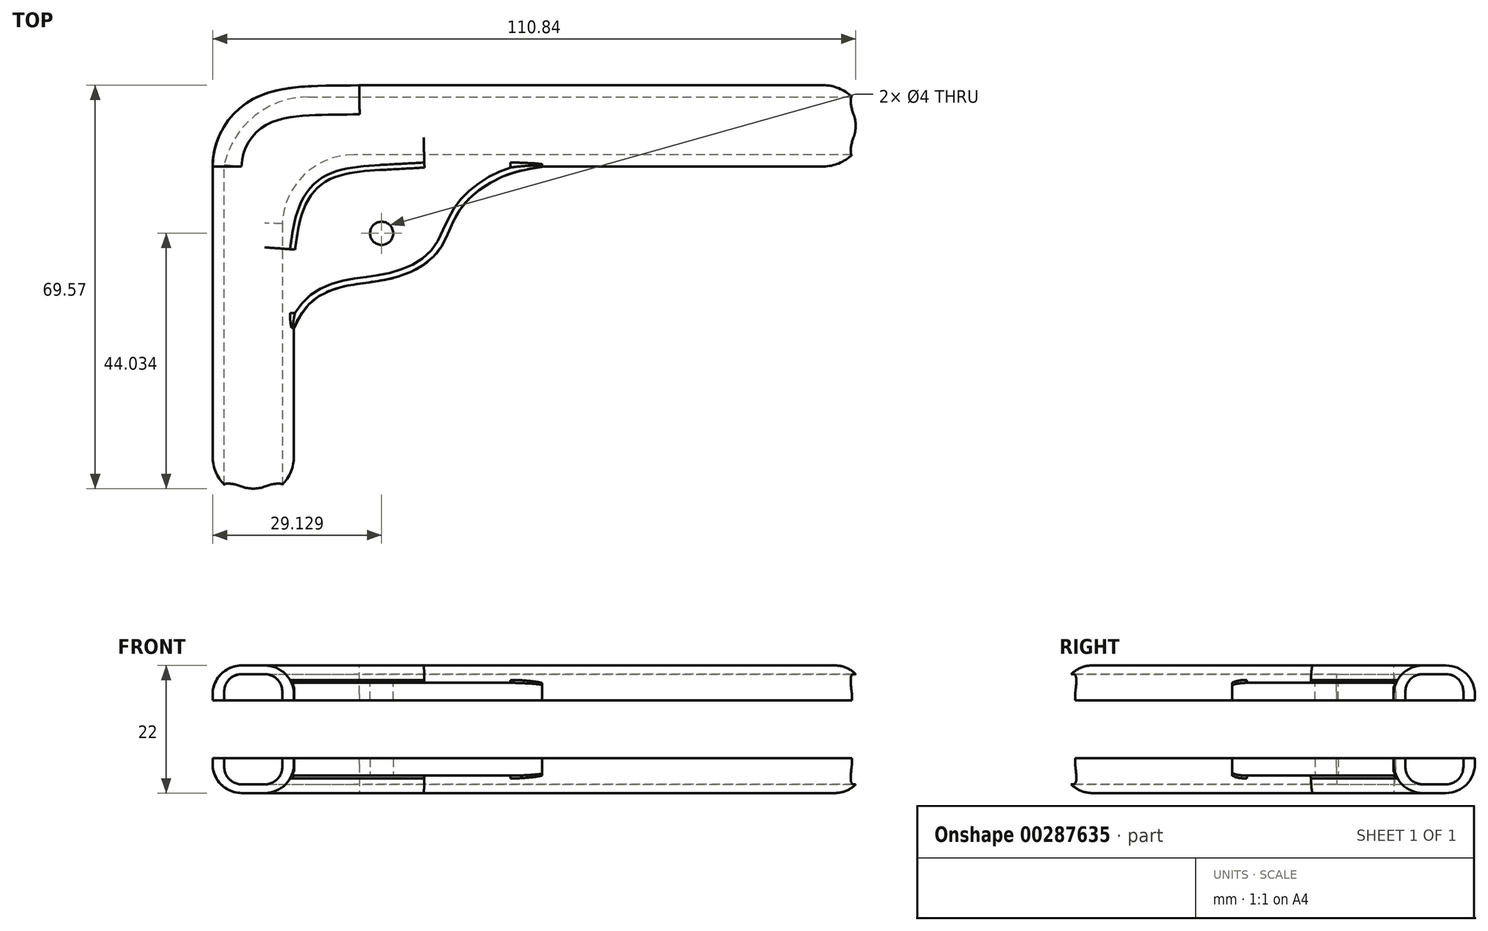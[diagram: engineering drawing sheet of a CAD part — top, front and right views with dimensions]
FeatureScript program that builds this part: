
annotation { "Feature Type Name" : "Feature", "Feature Type Description" : "" }
export const myFeature = defineFeature(function(context is Context, id is Id, definition is map)
    precondition{}
    {
        {
            var Q0;
            Q0=qCreatedBy(makeId("Top.planeOp"),FACE);
            var sketch = newSketch(context, id + "F0", { "sketchPlane" : qUnion([Q0])});
            skLineSegment(sketch, "E0", {"start": v(-18.78, 30.81) * mm, "end": v(61.22, 30.81) * mm});
            skLineSegment(sketch, "E1", {"start": v(61.22, 16.81) * mm, "end": v(-15.24, 16.81) * mm});
            skLineSegment(sketch, "E2", {"start": v(-30.05, 5.31) * mm, "end": v(-30.05, -33.19) * mm});
            skLineSegment(sketch, "E3", {"start": v(-44.05, -33.19) * mm, "end": v(-44.05, 16.81) * mm});
            skFitSpline(sketch, "E4", {"points": [v(-44.05, 16.81) * mm, v(-36.96, 28.5) * mm, v(-18.78, 30.81) * mm], "startDerivative": vector(-0.17, 32.3) * mm, "endDerivative": vector(38.07, 0.9) * mm});
            skFitSpline(sketch, "E5", {"points": [v(-30.05, 5.31) * mm, v(-26.31, 13.67) * mm, v(-15.24, 16.81) * mm], "startDerivative": vector(3.69, 24.67) * mm, "endDerivative": vector(33.65, 1.83) * mm});
            skArc(sketch, "E6", {"start": v(61.22, 16.81) * mm, "mid": v(68.22, 23.81) * mm, "end": v(61.22, 30.81) * mm});
            skArc(sketch, "E7", {"start": v(-44.05, -33.19) * mm, "mid": v(-37.05, -40.19) * mm, "end": v(-30.05, -33.19) * mm});
            skSolve(sketch);
        }
        {
            var Q0;
            Q0=qSketchRegion(id+"F0",true);
            extrude(context, id + "F1", {"entities" : qUnion([Q0]), "depth" : 6 * mm});
        }
        {
            var Q0;
            Q0=makeQuery(id+"F1.opExtrude","CAP_FACE",FACE,{"disambiguationData":[OSD([sQuery(id+"F0.wireOp",EDGE,"E0"),sQuery(id+"F0.wireOp",EDGE,"E1"),sQuery(id+"F0.wireOp",EDGE,"E2"),sQuery(id+"F0.wireOp",EDGE,"E3"),sQuery(id+"F0.wireOp",EDGE,"E4"),sQuery(id+"F0.wireOp",EDGE,"E5"),sQuery(id+"F0.wireOp",EDGE,"E6"),sQuery(id+"F0.wireOp",EDGE,"E7")])],"isStart":true});
            var sketch = newSketch(context, id + "F2", { "sketchPlane" : qUnion([Q0])});
            skLineSegment(sketch, "E8", {"start": v(-42.05, 45.95) * mm, "end": v(-42.05, -17.13) * mm});
            skLineSegment(sketch, "E9", {"start": v(-27.44, -28.81) * mm, "end": v(78.08, -28.81) * mm});
            skLineSegment(sketch, "E10", {"start": v(78.08, -28.81) * mm, "end": v(78.08, -18.81) * mm});
            skLineSegment(sketch, "E11", {"start": v(78.08, -18.81) * mm, "end": v(-19.7, -18.81) * mm});
            skLineSegment(sketch, "E12", {"start": v(-32.05, -6.95) * mm, "end": v(-32.05, 45.95) * mm});
            skLineSegment(sketch, "E13", {"start": v(-32.05, 45.95) * mm, "end": v(-42.05, 45.95) * mm});
            skPoint(sketch, "E14.end.orphan", {"position": v(-27.44, -17.13) * mm});
            skArc(sketch, "E15", {"start": v(-32.05, -6.95) * mm, "mid": v(-28.26, -15.37) * mm, "end": v(-19.7, -18.81) * mm});
            skArc(sketch, "E16", {"start": v(-42.05, -17.13) * mm, "mid": v(-36.8, -25.53) * mm, "end": v(-27.44, -28.81) * mm});
            skSolve(sketch);
        }
        {
            var Q0;
            {var subQ0=sQuery(id+"F2.wireOp",EDGE,"E15");Q0=makeQuery(id+"F2.imprint","IMPRINT",FACE,{"disambiguationData":[TD([[makeQuery(id+"F2.imprint","IMPRINT",EDGE,{"derivedFrom":subQ0}),-1.0]])]});}
            extrude(context, id + "F3", {"entities" : qUnion([Q0]), "operationType" : NewBodyOperationType.REMOVE, "oppositeDirection" : true, "depth" : 4.5 * mm});
        }
        {
            var Q0;
            Q0=makeQuery(id+"F3.boolean.opBoolean","COPY",EDGE,{"derivedFrom":makeQuery(id+"F3.opExtrude","CAP_EDGE",EDGE,{"disambiguationData":[OSD([sQuery(id+"F2.wireOp",EDGE,"E12")])],"isStart":false})});
            var Q1;
            Q1=makeQuery(id+"F3.boolean.opBoolean","COPY",EDGE,{"derivedFrom":makeQuery(id+"F3.opExtrude","CAP_EDGE",EDGE,{"disambiguationData":[OSD([sQuery(id+"F2.wireOp",EDGE,"E15")])],"isStart":false})});
            var Q2;
            Q2=makeQuery(id+"F3.boolean.opBoolean","COPY",EDGE,{"derivedFrom":makeQuery(id+"F3.opExtrude","CAP_EDGE",EDGE,{"disambiguationData":[OSD([sQuery(id+"F2.wireOp",EDGE,"E11")])],"isStart":false})});
            var Q3;
            Q3=makeQuery(id+"F3.boolean.opBoolean","COPY",EDGE,{"derivedFrom":makeQuery(id+"F3.opExtrude","CAP_EDGE",EDGE,{"disambiguationData":[OSD([sQuery(id+"F2.wireOp",EDGE,"E8")])],"isStart":false})});
            var Q4;
            Q4=makeQuery(id+"F3.boolean.opBoolean","COPY",EDGE,{"derivedFrom":makeQuery(id+"F3.opExtrude","CAP_EDGE",EDGE,{"disambiguationData":[OSD([sQuery(id+"F2.wireOp",EDGE,"E16")])],"isStart":false})});
            var Q5;
            Q5=makeQuery(id+"F3.boolean.opBoolean","COPY",EDGE,{"derivedFrom":makeQuery(id+"F3.opExtrude","CAP_EDGE",EDGE,{"disambiguationData":[OSD([sQuery(id+"F2.wireOp",EDGE,"E9")])],"isStart":false})});
            fillet(context, id + "F4", {"entities" : qUnion([Q0, Q1, Q2, Q3, Q4, Q5]), "radius" : 3 * mm, "tangentPropagation" : true, "allowEdgeOverflow" : false});
        }
        {
            var Q0;
            Q0=qCreatedBy(makeId("Top.planeOp"),FACE);
            var sketch = newSketch(context, id + "F5", { "sketchPlane" : qUnion([Q0])});
            skFitSpline(sketch, "E17", {"points": [v(-30, -11) * mm, v(-22.95, -4.29) * mm, v(-12.98, -2.43) * mm, v(-5.33, 1.97) * mm, v(-1.81, 8.75) * mm, v(3.65, 13.92) * mm, v(12.75, 16.76) * mm], "startDerivative": vector(29.59, 69.04) * mm, "endDerivative": vector(74.32, 11.2) * mm});
            skLineSegment(sketch, "E18", {"start": v(-30, -11) * mm, "end": v(-31.06, -11) * mm});
            skLineSegment(sketch, "E19", {"start": v(-31.06, -11) * mm, "end": v(-31.06, 6.62) * mm});
            skLineSegment(sketch, "E20", {"start": v(-31.06, 6.62) * mm, "end": v(-29.27, 11.9) * mm});
            skLineSegment(sketch, "E21", {"start": v(-29.27, 11.9) * mm, "end": v(-25.9, 15.43) * mm});
            skLineSegment(sketch, "E22", {"start": v(-25.9, 15.43) * mm, "end": v(-21.38, 17) * mm});
            skLineSegment(sketch, "E23", {"start": v(-21.38, 17) * mm, "end": v(-16.05, 17.63) * mm});
            skLineSegment(sketch, "E24", {"start": v(-16.05, 17.63) * mm, "end": v(12.75, 17.63) * mm});
            skLineSegment(sketch, "E25", {"start": v(12.75, 17.63) * mm, "end": v(12.75, 16.76) * mm});
            skSolve(sketch);
        }
        {
            var Q0;
            Q0=qSketchRegion(id+"F5",true);
            extrude(context, id + "F6", {"entities" : qUnion([Q0]), "operationType" : NewBodyOperationType.ADD, "depth" : 3 * mm});
        }
        {
            var Q0;
            Q0=makeQuery(id+"F1.opExtrude","CAP_EDGE",EDGE,{"disambiguationData":[OSD([sQuery(id+"F0.wireOp",EDGE,"E3")])],"isStart":false});
            var Q1;
            Q1=makeQuery(id+"F1.opExtrude","CAP_EDGE",EDGE,{"disambiguationData":[OSD([sQuery(id+"F0.wireOp",EDGE,"E4")])],"isStart":false});
            var Q2;
            Q2=makeQuery(id+"F1.opExtrude","CAP_EDGE",EDGE,{"disambiguationData":[OSD([sQuery(id+"F0.wireOp",EDGE,"E0")])],"isStart":false});
            var Q3;
            Q3=makeQuery(id+"F1.opExtrude","CAP_EDGE",EDGE,{"disambiguationData":[OSD([sQuery(id+"F0.wireOp",EDGE,"E6")])],"isStart":false});
            var Q4;
            Q4=makeQuery(id+"F1.opExtrude","CAP_EDGE",EDGE,{"disambiguationData":[OSD([sQuery(id+"F0.wireOp",EDGE,"E1")])],"isStart":false});
            var Q5;
            Q5=makeQuery(id+"F1.opExtrude","CAP_EDGE",EDGE,{"disambiguationData":[OSD([sQuery(id+"F0.wireOp",EDGE,"E5")])],"isStart":false});
            var Q6;
            Q6=makeQuery(id+"F1.opExtrude","CAP_EDGE",EDGE,{"disambiguationData":[OSD([sQuery(id+"F0.wireOp",EDGE,"E2")])],"isStart":false});
            var Q7;
            Q7=makeQuery(id+"F1.opExtrude","CAP_EDGE",EDGE,{"disambiguationData":[OSD([sQuery(id+"F0.wireOp",EDGE,"E7")])],"isStart":false});
            fillet(context, id + "F7", {"entities" : qUnion([Q0, Q1, Q2, Q3, Q4, Q5, Q6, Q7]), "radius" : 5 * mm, "tangentPropagation" : true, "allowEdgeOverflow" : false});
        }
        {
            var Q0;
            Q0=makeQuery(id+"F6.opExtrude","CAP_EDGE",EDGE,{"disambiguationData":[OSD([sQuery(id+"F5.wireOp",EDGE,"E17")])],"isStart":false});
            fillet(context, id + "F8", {"entities" : qUnion([Q0]), "radius" : 1 * mm, "tangentPropagation" : true, "allowEdgeOverflow" : false});
        }
        {
            var Q0;
            Q0=makeQuery(id+"F6.opExtrude","CAP_FACE",FACE,{"disambiguationData":[OSD([sQuery(id+"F5.wireOp",EDGE,"E17"),sQuery(id+"F5.wireOp",EDGE,"E18"),sQuery(id+"F5.wireOp",EDGE,"E19"),sQuery(id+"F5.wireOp",EDGE,"E20"),sQuery(id+"F5.wireOp",EDGE,"E21"),sQuery(id+"F5.wireOp",EDGE,"E22"),sQuery(id+"F5.wireOp",EDGE,"E23"),sQuery(id+"F5.wireOp",EDGE,"E24"),sQuery(id+"F5.wireOp",EDGE,"E25")])],"isStart":false});
            var sketch = newSketch(context, id + "F9", { "sketchPlane" : qUnion([Q0])});
            skCircle(sketch, "E26", {"center": v(-14.92, 5.27) * mm, "radius": 2 * mm});
            skSolve(sketch);
        }
        {
            var Q0;
            Q0=qSketchRegion(id+"F9",true);
            extrude(context, id + "F10", {"entities" : qUnion([Q0]), "operationType" : NewBodyOperationType.REMOVE, "endBound" : BoundingType.THROUGH_ALL, "oppositeDirection" : true, "depth" : 25 * mm});
        }
        {
            var Q0;
            Q0=makeQuery(id+"F7.opFillet","BLEND_EDGE",EDGE,{"blendedFrom":[makeQuery(id+"F1.opExtrude","CAP_EDGE",EDGE,{"disambiguationData":[OSD([sQuery(id+"F0.wireOp",EDGE,"E1")])],"isStart":false}),makeQuery(id+"F6.opExtrude","CAP_FACE",FACE,{"disambiguationData":[OSD([sQuery(id+"F5.wireOp",EDGE,"E17"),sQuery(id+"F5.wireOp",EDGE,"E18"),sQuery(id+"F5.wireOp",EDGE,"E19"),sQuery(id+"F5.wireOp",EDGE,"E20"),sQuery(id+"F5.wireOp",EDGE,"E21"),sQuery(id+"F5.wireOp",EDGE,"E22"),sQuery(id+"F5.wireOp",EDGE,"E23"),sQuery(id+"F5.wireOp",EDGE,"E24"),sQuery(id+"F5.wireOp",EDGE,"E25")])],"isStart":false})],"blendedInto":[makeQuery(id+"F6.opExtrude","CAP_FACE",FACE,{"disambiguationData":[OSD([sQuery(id+"F5.wireOp",EDGE,"E17"),sQuery(id+"F5.wireOp",EDGE,"E18"),sQuery(id+"F5.wireOp",EDGE,"E19"),sQuery(id+"F5.wireOp",EDGE,"E20"),sQuery(id+"F5.wireOp",EDGE,"E21"),sQuery(id+"F5.wireOp",EDGE,"E22"),sQuery(id+"F5.wireOp",EDGE,"E23"),sQuery(id+"F5.wireOp",EDGE,"E24"),sQuery(id+"F5.wireOp",EDGE,"E25")])],"isStart":false})]});
            var Q1;
            Q1=makeQuery(id+"F7.opFillet","BLEND_EDGE",EDGE,{"disambiguationData":[OD(0.0)],"blendedFrom":[makeQuery(id+"F1.opExtrude","CAP_EDGE",EDGE,{"disambiguationData":[OSD([sQuery(id+"F0.wireOp",EDGE,"E5")])],"isStart":false}),makeQuery(id+"F6.opExtrude","CAP_FACE",FACE,{"disambiguationData":[OSD([sQuery(id+"F5.wireOp",EDGE,"E17"),sQuery(id+"F5.wireOp",EDGE,"E18"),sQuery(id+"F5.wireOp",EDGE,"E19"),sQuery(id+"F5.wireOp",EDGE,"E20"),sQuery(id+"F5.wireOp",EDGE,"E21"),sQuery(id+"F5.wireOp",EDGE,"E22"),sQuery(id+"F5.wireOp",EDGE,"E23"),sQuery(id+"F5.wireOp",EDGE,"E24"),sQuery(id+"F5.wireOp",EDGE,"E25")])],"isStart":false})],"blendedInto":[makeQuery(id+"F6.opExtrude","CAP_FACE",FACE,{"disambiguationData":[OSD([sQuery(id+"F5.wireOp",EDGE,"E17"),sQuery(id+"F5.wireOp",EDGE,"E18"),sQuery(id+"F5.wireOp",EDGE,"E19"),sQuery(id+"F5.wireOp",EDGE,"E20"),sQuery(id+"F5.wireOp",EDGE,"E21"),sQuery(id+"F5.wireOp",EDGE,"E22"),sQuery(id+"F5.wireOp",EDGE,"E23"),sQuery(id+"F5.wireOp",EDGE,"E24"),sQuery(id+"F5.wireOp",EDGE,"E25")])],"isStart":false})]});
            var Q2;
            Q2=makeQuery(id+"F7.opFillet","BLEND_EDGE",EDGE,{"disambiguationData":[OD(2.0)],"blendedFrom":[makeQuery(id+"F1.opExtrude","CAP_EDGE",EDGE,{"disambiguationData":[OSD([sQuery(id+"F0.wireOp",EDGE,"E5")])],"isStart":false}),makeQuery(id+"F6.opExtrude","CAP_FACE",FACE,{"disambiguationData":[OSD([sQuery(id+"F5.wireOp",EDGE,"E17"),sQuery(id+"F5.wireOp",EDGE,"E18"),sQuery(id+"F5.wireOp",EDGE,"E19"),sQuery(id+"F5.wireOp",EDGE,"E20"),sQuery(id+"F5.wireOp",EDGE,"E21"),sQuery(id+"F5.wireOp",EDGE,"E22"),sQuery(id+"F5.wireOp",EDGE,"E23"),sQuery(id+"F5.wireOp",EDGE,"E24"),sQuery(id+"F5.wireOp",EDGE,"E25")])],"isStart":false})],"blendedInto":[makeQuery(id+"F6.opExtrude","CAP_FACE",FACE,{"disambiguationData":[OSD([sQuery(id+"F5.wireOp",EDGE,"E17"),sQuery(id+"F5.wireOp",EDGE,"E18"),sQuery(id+"F5.wireOp",EDGE,"E19"),sQuery(id+"F5.wireOp",EDGE,"E20"),sQuery(id+"F5.wireOp",EDGE,"E21"),sQuery(id+"F5.wireOp",EDGE,"E22"),sQuery(id+"F5.wireOp",EDGE,"E23"),sQuery(id+"F5.wireOp",EDGE,"E24"),sQuery(id+"F5.wireOp",EDGE,"E25")])],"isStart":false})]});
            var Q3;
            Q3=makeQuery(id+"F7.opFillet","BLEND_EDGE",EDGE,{"disambiguationData":[OD(1.0)],"blendedFrom":[makeQuery(id+"F1.opExtrude","CAP_EDGE",EDGE,{"disambiguationData":[OSD([sQuery(id+"F0.wireOp",EDGE,"E5")])],"isStart":false}),makeQuery(id+"F6.opExtrude","CAP_FACE",FACE,{"disambiguationData":[OSD([sQuery(id+"F5.wireOp",EDGE,"E17"),sQuery(id+"F5.wireOp",EDGE,"E18"),sQuery(id+"F5.wireOp",EDGE,"E19"),sQuery(id+"F5.wireOp",EDGE,"E20"),sQuery(id+"F5.wireOp",EDGE,"E21"),sQuery(id+"F5.wireOp",EDGE,"E22"),sQuery(id+"F5.wireOp",EDGE,"E23"),sQuery(id+"F5.wireOp",EDGE,"E24"),sQuery(id+"F5.wireOp",EDGE,"E25")])],"isStart":false})],"blendedInto":[makeQuery(id+"F6.opExtrude","CAP_FACE",FACE,{"disambiguationData":[OSD([sQuery(id+"F5.wireOp",EDGE,"E17"),sQuery(id+"F5.wireOp",EDGE,"E18"),sQuery(id+"F5.wireOp",EDGE,"E19"),sQuery(id+"F5.wireOp",EDGE,"E20"),sQuery(id+"F5.wireOp",EDGE,"E21"),sQuery(id+"F5.wireOp",EDGE,"E22"),sQuery(id+"F5.wireOp",EDGE,"E23"),sQuery(id+"F5.wireOp",EDGE,"E24"),sQuery(id+"F5.wireOp",EDGE,"E25")])],"isStart":false})]});
            var Q4;
            Q4=makeQuery(id+"F7.opFillet","BLEND_EDGE",EDGE,{"blendedFrom":[makeQuery(id+"F1.opExtrude","CAP_EDGE",EDGE,{"disambiguationData":[OSD([sQuery(id+"F0.wireOp",EDGE,"E2")])],"isStart":false}),makeQuery(id+"F6.opExtrude","CAP_FACE",FACE,{"disambiguationData":[OSD([sQuery(id+"F5.wireOp",EDGE,"E17"),sQuery(id+"F5.wireOp",EDGE,"E18"),sQuery(id+"F5.wireOp",EDGE,"E19"),sQuery(id+"F5.wireOp",EDGE,"E20"),sQuery(id+"F5.wireOp",EDGE,"E21"),sQuery(id+"F5.wireOp",EDGE,"E22"),sQuery(id+"F5.wireOp",EDGE,"E23"),sQuery(id+"F5.wireOp",EDGE,"E24"),sQuery(id+"F5.wireOp",EDGE,"E25")])],"isStart":false})],"blendedInto":[makeQuery(id+"F6.opExtrude","CAP_FACE",FACE,{"disambiguationData":[OSD([sQuery(id+"F5.wireOp",EDGE,"E17"),sQuery(id+"F5.wireOp",EDGE,"E18"),sQuery(id+"F5.wireOp",EDGE,"E19"),sQuery(id+"F5.wireOp",EDGE,"E20"),sQuery(id+"F5.wireOp",EDGE,"E21"),sQuery(id+"F5.wireOp",EDGE,"E22"),sQuery(id+"F5.wireOp",EDGE,"E23"),sQuery(id+"F5.wireOp",EDGE,"E24"),sQuery(id+"F5.wireOp",EDGE,"E25")])],"isStart":false})]});
            fillet(context, id + "F11", {"entities" : qUnion([Q0, Q1, Q2, Q3, Q4]), "radius" : 1 * mm, "tangentPropagation" : true, "allowEdgeOverflow" : false});
        }
        {
            var Q0;
            Q0=qCreatedBy(makeId("Top.planeOp"),FACE);
            cPlane(context, id + "F12", {"entities" : qUnion([Q0]), "cplaneType" : CPlaneType.OFFSET, "offset" : 5 * mm, "oppositeDirection" : true, "width" : 150 * mm, "height" : 150 * mm});
        }
        {
            var Q0;
            Q0=makeQuery(id+"F1.opExtrude","SWEPT_BODY",BODY,{"disambiguationData":[OSD([sQuery(id+"F0.wireOp",EDGE,"E0"),sQuery(id+"F0.wireOp",EDGE,"E1"),sQuery(id+"F0.wireOp",EDGE,"E2"),sQuery(id+"F0.wireOp",EDGE,"E3"),sQuery(id+"F0.wireOp",EDGE,"E4"),sQuery(id+"F0.wireOp",EDGE,"E5"),sQuery(id+"F0.wireOp",EDGE,"E6"),sQuery(id+"F0.wireOp",EDGE,"E7")])]});
            var Q1;
            Q1=qCreatedBy(id+"F12.planeOp",FACE);
            mirror(context, id + "F13", {"entities" : qUnion([Q0]), "mirrorPlane" : qUnion([Q1])});
        }
    });
